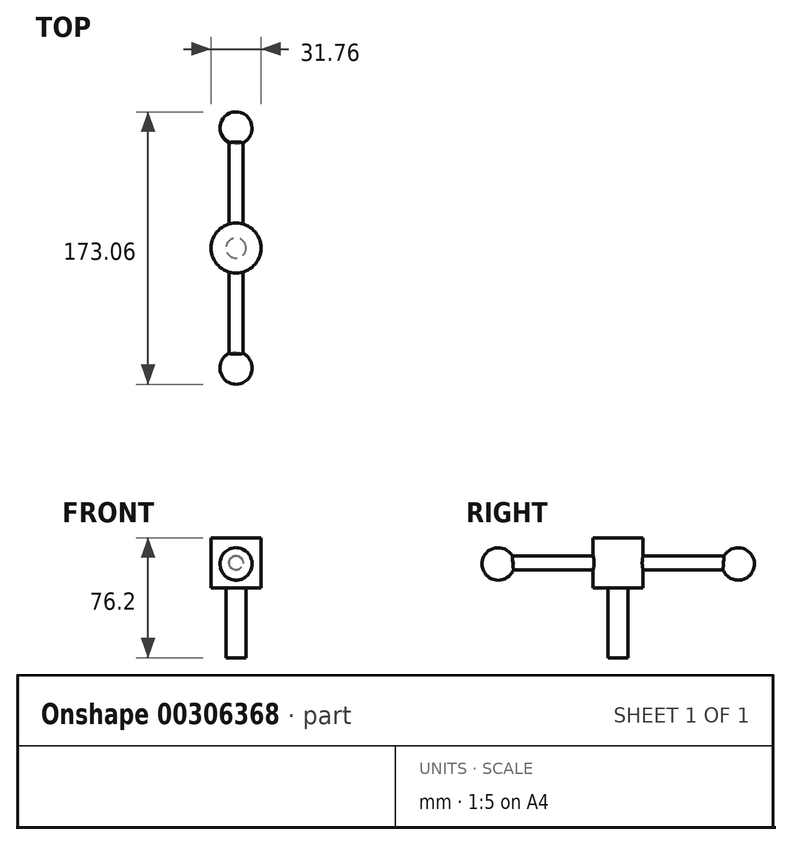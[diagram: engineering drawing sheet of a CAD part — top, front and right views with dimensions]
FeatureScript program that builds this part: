
annotation { "Feature Type Name" : "Feature", "Feature Type Description" : "" }
export const myFeature = defineFeature(function(context is Context, id is Id, definition is map)
    precondition{}
    {
        {
            var Q0;
            Q0=qCreatedBy(makeId("Top.planeOp"),FACE);
            var sketch = newSketch(context, id + "F0", { "sketchPlane" : qUnion([Q0])});
            skCircle(sketch, "E0", {"center": v(0, 0) * mm, "radius": 15.88 * mm});
            skSolve(sketch);
        }
        {
            var Q0;
            Q0 = qSketchRegion(id + "F0", true);
            extrude(context, id + "F1", {"entities" : qUnion([Q0]), "depth" : 31.75 * mm});
        }
        {
            var Q0;
            Q0=qCreatedBy(makeId("Front.planeOp"),FACE);
            var sketch = newSketch(context, id + "F2", { "sketchPlane" : qUnion([Q0])});
            skCircle(sketch, "E1", {"center": v(0, 15.88) * mm, "radius": 4.45 * mm});
            skSolve(sketch);
        }
        {
            var Q0;
            Q0 = qSketchRegion(id + "F2", true);
            extrude(context, id + "F3", {"entities" : qUnion([Q0]), "operationType" : NewBodyOperationType.ADD, "depth" : 76.2 * mm});
        }
        {
            var Q0;
            Q0=makeQuery(id+"F1.opExtrude","SWEPT_BODY",BODY,{"disambiguationData":[OSD([sQuery(id+"F0.wireOp",EDGE,"E0")])]});
            var Q1;
            Q1=qCreatedBy(makeId("Front.planeOp"),FACE);
            mirror(context, id + "F4", {"operationType" : NewBodyOperationType.ADD, "entities" : qUnion([Q0]), "mirrorPlane" : qUnion([Q1])});
        }
        {
            var Q0;
            Q0=makeQuery(id+"F3.opExtrude","CAP_FACE",FACE,{"disambiguationData":[OSD([sQuery(id+"F2.wireOp",EDGE,"E1")])],"isStart":false});
            cPlane(context, id + "F5", {"entities" : qUnion([Q0]), "cplaneType" : CPlaneType.OFFSET, "offset" : 0 * mm, "width" : 152.4 * mm, "height" : 152.4 * mm});
        }
        {
            var Q0;
            Q0=qCreatedBy(id+"F5.planeOp",FACE);
            var sketch = newSketch(context, id + "F6", { "sketchPlane" : qUnion([Q0])});
            skArc(sketch, "E2", {"start": v(10.16, 15.13) * mm, "mid": v(0, 25.46) * mm, "end": v(-10.16, 15.13) * mm});
            skLineSegment(sketch, "E3", {"start": v(-10.16, 15.13) * mm, "end": v(10.16, 15.13) * mm});
            skSolve(sketch);
        }
        {
            var Q0;
            Q0=makeQuery(id+"F6.imprint","IMPRINT",FACE,{"disambiguationData":[TD([[makeQuery(id+"F6.imprint","IMPRINT",EDGE,{"derivedFrom":sQuery(id+"F6.wireOp",EDGE,"E2")}),1.0]])]});
            var Q1;
            Q1=sQuery(id+"F6.wireOp",EDGE,"E3");
            revolve(context, id + "F7", {"entities" : qUnion([Q0]), "axis" : qUnion([Q1]), "revolveType" : RevolveType.FULL});
        }
        {
            var Q0;
            Q0=makeQuery(id+"F7.opRevolve","SWEPT_BODY",BODY,{"disambiguationData":[OSD([sQuery(id+"F6.wireOp",EDGE,"E2"),sQuery(id+"F6.wireOp",EDGE,"E3")])]});
            var Q1;
            Q1=qCreatedBy(makeId("Front.planeOp"),FACE);
            mirror(context, id + "F8", {"operationType" : NewBodyOperationType.ADD, "entities" : qUnion([Q0]), "mirrorPlane" : qUnion([Q1])});
        }
        {
            var Q0;
            Q0=makeQuery(id+"F1.opExtrude","CAP_FACE",FACE,{"disambiguationData":[OSD([sQuery(id+"F0.wireOp",EDGE,"E0")])],"isStart":true});
            var sketch = newSketch(context, id + "F9", { "sketchPlane" : qUnion([Q0])});
            skCircle(sketch, "E4", {"center": v(0, 0) * mm, "radius": 6.35 * mm});
            skSolve(sketch);
        }
        {
            var Q0;
            Q0 = qSketchRegion(id + "F9", true);
            extrude(context, id + "F10", {"entities" : qUnion([Q0]), "operationType" : NewBodyOperationType.ADD, "depth" : 44.45 * mm});
        }
    });
